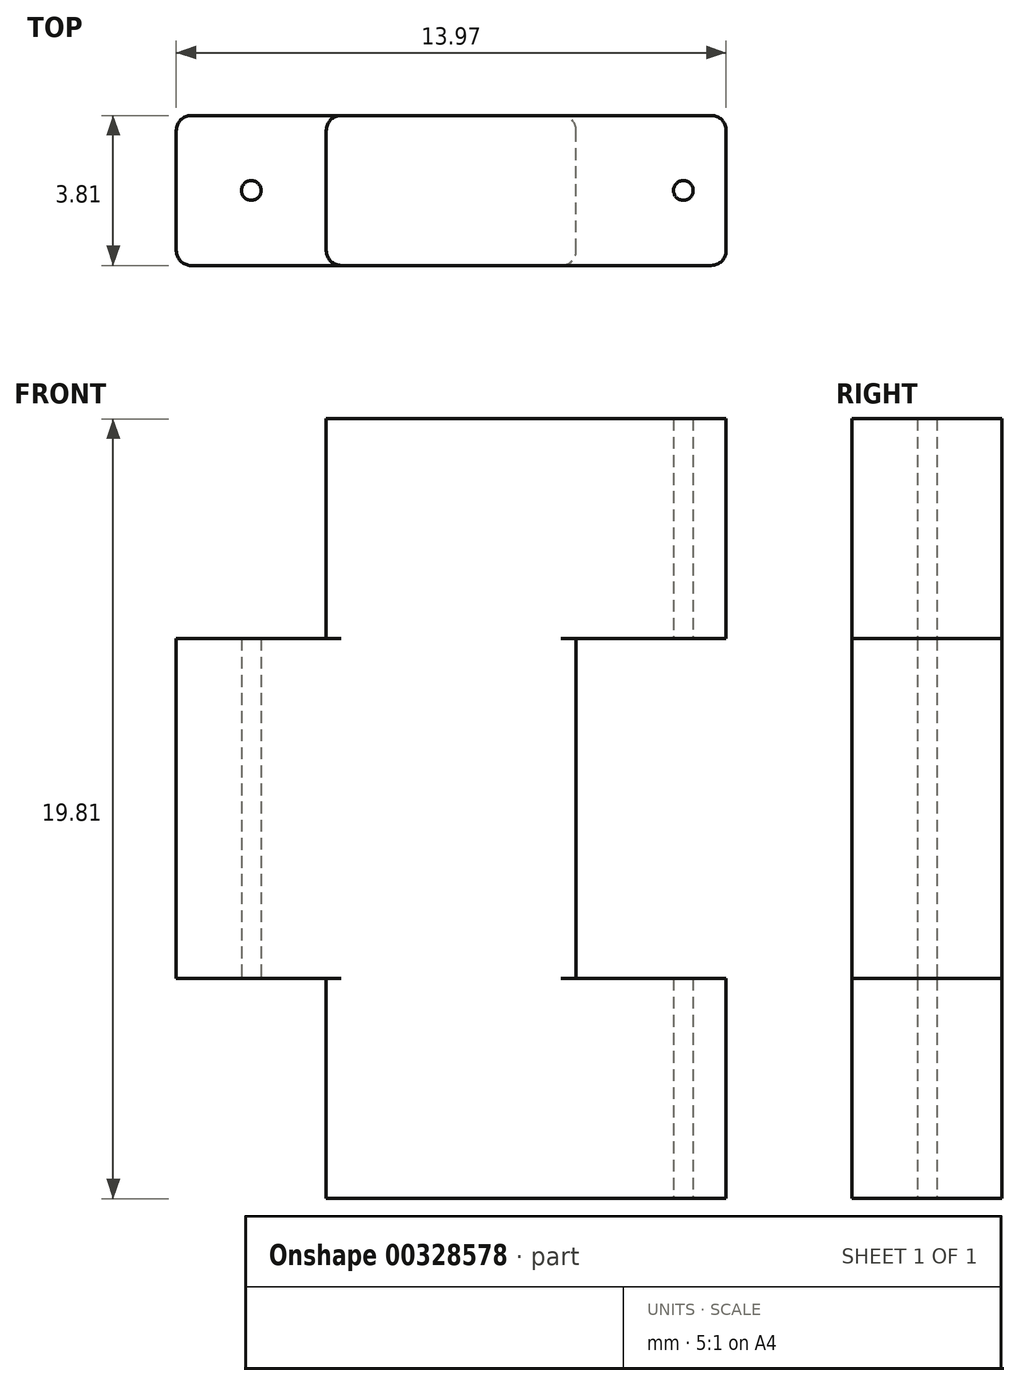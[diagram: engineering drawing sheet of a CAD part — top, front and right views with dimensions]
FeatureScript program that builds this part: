
annotation { "Feature Type Name" : "Feature", "Feature Type Description" : "" }
export const myFeature = defineFeature(function(context is Context, id is Id, definition is map)
    precondition{}
    {
        {
            var Q0;
            Q0=qCreatedBy(makeId("Front.planeOp"),FACE);
            var sketch = newSketch(context, id + "F0", { "sketchPlane" : qUnion([Q0])});
            skLineSegment(sketch, "E0.bottom", {"start": v(17.02, -29.15) * mm, "end": v(27.18, -29.15) * mm});
            skLineSegment(sketch, "E0.top", {"start": v(17.02, -48.96) * mm, "end": v(27.18, -48.96) * mm});
            skLineSegment(sketch, "E0.left", {"start": v(17.02, -29.15) * mm, "end": v(17.02, -34.73) * mm});
            skLineSegment(sketch, "E0.right", {"start": v(27.18, -29.15) * mm, "end": v(27.18, -34.73) * mm});
            skLineSegment(sketch, "E1", {"start": v(17.02, -48.96) * mm, "end": v(23.37, -48.96) * mm});
            skLineSegment(sketch, "E2", {"start": v(23.37, -43.37) * mm, "end": v(23.37, -34.73) * mm});
            skLineSegment(sketch, "E3", {"start": v(27.18, -34.73) * mm, "end": v(23.37, -34.73) * mm});
            skLineSegment(sketch, "E4", {"start": v(27.18, -48.96) * mm, "end": v(27.18, -43.37) * mm});
            skLineSegment(sketch, "E5", {"start": v(27.18, -43.37) * mm, "end": v(23.37, -43.37) * mm});
            skLineSegment(sketch, "E6.trimOffspring", {"start": v(27.18, -43.37) * mm, "end": v(27.18, -48.96) * mm});
            skLineSegment(sketch, "E7", {"start": v(17.02, -43.37) * mm, "end": v(13.21, -43.37) * mm});
            skLineSegment(sketch, "E8", {"start": v(13.21, -43.37) * mm, "end": v(13.21, -34.73) * mm});
            skLineSegment(sketch, "E9", {"start": v(13.21, -34.73) * mm, "end": v(17.02, -34.73) * mm});
            skLineSegment(sketch, "E10.trimOffspring", {"start": v(17.02, -43.37) * mm, "end": v(17.02, -48.96) * mm});
            skLineSegment(sketch, "E11", {"start": v(17.02, -43.37) * mm, "end": v(23.37, -43.37) * mm});
            skLineSegment(sketch, "E12", {"start": v(23.37, -34.73) * mm, "end": v(17.02, -34.73) * mm});
            skSolve(sketch);
        }
        {
            var Q0;
            Q0=makeQuery(id+"F0.imprint","IMPRINT",FACE,{"disambiguationData":[TD([[makeQuery(id+"F0.imprint","IMPRINT",EDGE,{"derivedFrom":sQuery(id+"F0.wireOp",EDGE,"E2")}),1.0]])]});
            extrude(context, id + "F1", {"entities" : qUnion([Q0]), "depth" : 3.8 * mm});
        }
        {
            var Q0;
            Q0=makeQuery(id+"F1.opExtrude","CAP_FACE",FACE,{"disambiguationData":[OSD([sQuery(id+"F0.wireOp",EDGE,"E2"),sQuery(id+"F0.wireOp",EDGE,"E7"),sQuery(id+"F0.wireOp",EDGE,"E8"),sQuery(id+"F0.wireOp",EDGE,"E9"),sQuery(id+"F0.wireOp",EDGE,"E11"),sQuery(id+"F0.wireOp",EDGE,"E12")])],"isStart":false});
            var sketch = newSketch(context, id + "F2", { "sketchPlane" : qUnion([Q0])});
            skLineSegment(sketch, "E13.bottom", {"start": v(17.02, -29.15) * mm, "end": v(27.18, -29.15) * mm});
            skLineSegment(sketch, "E13.left", {"start": v(17.02, -29.15) * mm, "end": v(17.02, -34.73) * mm});
            skLineSegment(sketch, "E14", {"start": v(27.18, -29.15) * mm, "end": v(27.18, -34.73) * mm});
            skLineSegment(sketch, "E15", {"start": v(27.18, -34.73) * mm, "end": v(23.37, -34.73) * mm});
            skLineSegment(sketch, "E16", {"start": v(23.37, -34.73) * mm, "end": v(17.02, -34.73) * mm});
            skLineSegment(sketch, "E17.MirrorCS", {"start": v(23.37, -43.37) * mm, "end": v(17.02, -43.37) * mm});
            skLineSegment(sketch, "E18.MirrorCS", {"start": v(27.18, -43.37) * mm, "end": v(23.37, -43.37) * mm});
            skLineSegment(sketch, "E19.MirrorCS", {"start": v(27.18, -48.96) * mm, "end": v(27.18, -43.37) * mm});
            skLineSegment(sketch, "E20.MirrorCS", {"start": v(17.02, -48.96) * mm, "end": v(17.02, -43.37) * mm});
            skLineSegment(sketch, "E21.MirrorCS", {"start": v(17.02, -48.96) * mm, "end": v(27.18, -48.96) * mm});
            skSolve(sketch);
        }
        {
            var Q0;
            Q0 = qSketchRegion(id + "F2", true);
            extrude(context, id + "F3", {"entities" : qUnion([Q0]), "operationType" : NewBodyOperationType.ADD, "oppositeDirection" : true, "depth" : 3.81 * mm, "hasSecondDirection" : true, "secondDirectionOppositeDirection" : true, "secondDirectionDepth" : 0 * mm});
        }
        {
            var Q0;
            Q0=makeQuery(id+"F3.opExtrude","SWEPT_FACE",FACE,{"disambiguationData":[OSD([sQuery(id+"F2.wireOp",EDGE,"E21.MirrorCS")])]});
            var sketch = newSketch(context, id + "F4", { "sketchPlane" : qUnion([Q0])});
            skCircle(sketch, "E22", {"center": v(26.1, 1.9) * mm, "radius": 0.25 * mm});
            skSolve(sketch);
        }
        {
            var Q0;
            Q0 = qSketchRegion(id + "F4", true);
            extrude(context, id + "F5", {"entities" : qUnion([Q0]), "operationType" : NewBodyOperationType.REMOVE, "oppositeDirection" : true, "depth" : 50.8 * mm});
        }
        {
            var Q0;
            Q0=makeQuery(id+"F3.opExtrude","CAP_EDGE",EDGE,{"disambiguationData":[OSD([sQuery(id+"F2.wireOp",EDGE,"E14")])],"isStart":true});
            var Q1;
            Q1=makeQuery(id+"F3.opExtrude","CAP_EDGE",EDGE,{"disambiguationData":[OSD([sQuery(id+"F2.wireOp",EDGE,"E13.left")])],"isStart":true});
            var Q2;
            Q2=makeQuery(id+"F3.opExtrude","CAP_EDGE",EDGE,{"disambiguationData":[OSD([sQuery(id+"F2.wireOp",EDGE,"E19.MirrorCS")])],"isStart":true});
            var Q3;
            Q3=makeQuery(id+"F3.opExtrude","CAP_EDGE",EDGE,{"disambiguationData":[OSD([sQuery(id+"F2.wireOp",EDGE,"E20.MirrorCS")])],"isStart":true});
            var Q4;
            Q4=makeQuery(id+"F1.opExtrude","CAP_EDGE",EDGE,{"disambiguationData":[OSD([sQuery(id+"F0.wireOp",EDGE,"E2")])],"isStart":false});
            var Q5;
            Q5=makeQuery(id+"F1.opExtrude","CAP_EDGE",EDGE,{"disambiguationData":[OSD([sQuery(id+"F0.wireOp",EDGE,"E8")])],"isStart":false});
            var Q6;
            Q6=makeQuery(id+"F1.opExtrude","CAP_EDGE",EDGE,{"disambiguationData":[OSD([sQuery(id+"F0.wireOp",EDGE,"E2")])],"isStart":true});
            var Q7;
            Q7=makeQuery(id+"F1.opExtrude","CAP_EDGE",EDGE,{"disambiguationData":[OSD([sQuery(id+"F0.wireOp",EDGE,"E8")])],"isStart":true});
            var Q8;
            Q8=makeQuery(id+"F3.opExtrude","CAP_EDGE",EDGE,{"disambiguationData":[OSD([sQuery(id+"F2.wireOp",EDGE,"E13.left")])],"isStart":false});
            var Q9;
            Q9=makeQuery(id+"F3.opExtrude","CAP_EDGE",EDGE,{"disambiguationData":[OSD([sQuery(id+"F2.wireOp",EDGE,"E14")])],"isStart":false});
            var Q10;
            Q10=makeQuery(id+"F3.opExtrude","CAP_EDGE",EDGE,{"disambiguationData":[OSD([sQuery(id+"F2.wireOp",EDGE,"E19.MirrorCS")])],"isStart":false});
            var Q11;
            Q11=makeQuery(id+"F3.opExtrude","CAP_EDGE",EDGE,{"disambiguationData":[OSD([sQuery(id+"F2.wireOp",EDGE,"E20.MirrorCS")])],"isStart":false});
            var Q12;
            Q12=makeQuery(id+"F3.boolean.opBoolean","MERGE",EDGE,{"derivedFrom":[makeQuery(id+"F1.opExtrude","CAP_EDGE",EDGE,{"disambiguationData":[OSD([sQuery(id+"F0.wireOp",EDGE,"E9"),sQuery(id+"F0.wireOp",EDGE,"E12")])],"isStart":false}),makeQuery(id+"F3.opExtrude","CAP_EDGE",EDGE,{"disambiguationData":[OSD([sQuery(id+"F2.wireOp",EDGE,"E15"),sQuery(id+"F2.wireOp",EDGE,"E16")])],"isStart":true})]});
            fillet(context, id + "F6", {"entities" : qUnion([Q0, Q1, Q2, Q3, Q4, Q5, Q6, Q7, Q8, Q9, Q10, Q11, Q12]), "radius" : 0.38 * mm, "tangentPropagation" : true, "allowEdgeOverflow" : false});
        }
        {
            var Q0;
            Q0=makeQuery(id+"F1.opExtrude","SWEPT_FACE",FACE,{"disambiguationData":[OSD([sQuery(id+"F0.wireOp",EDGE,"E7"),sQuery(id+"F0.wireOp",EDGE,"E11")])]});
            var sketch = newSketch(context, id + "F7", { "sketchPlane" : qUnion([Q0])});
            skCircle(sketch, "E23", {"center": v(15.12, 1.9) * mm, "radius": 0.25 * mm});
            skSolve(sketch);
        }
        {
            var Q0;
            Q0 = qSketchRegion(id + "F7", true);
            extrude(context, id + "F8", {"entities" : qUnion([Q0]), "operationType" : NewBodyOperationType.REMOVE, "oppositeDirection" : true, "depth" : 50.8 * mm});
        }
    });
